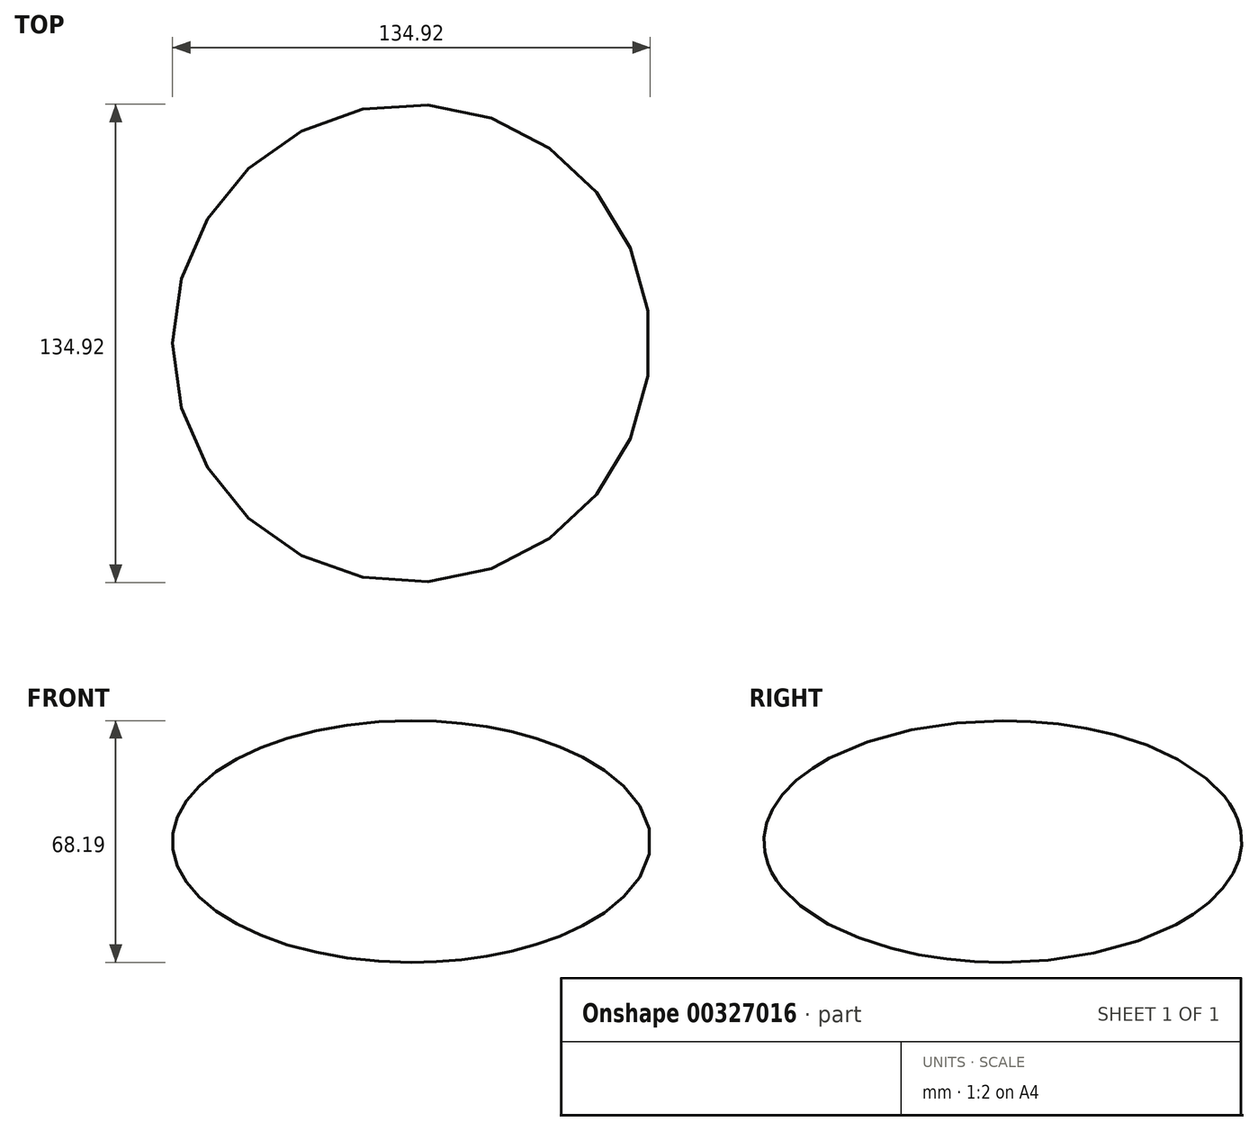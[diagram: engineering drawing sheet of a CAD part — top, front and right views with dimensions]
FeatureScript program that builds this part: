
annotation { "Feature Type Name" : "Feature", "Feature Type Description" : "" }
export const myFeature = defineFeature(function(context is Context, id is Id, definition is map)
    precondition{}
    {
        {
            var Q0;
            Q0=qCreatedBy(makeId("Front.planeOp"),FACE);
            var sketch = newSketch(context, id + "F0", { "sketchPlane" : qUnion([Q0])});
            skEllipse(sketch, "E0", {"center": v(0, 17.52) * mm, "majorRadius": 67.46 * mm, "minorRadius": 34.1 * mm, "majorAxis": v(1, 0)});
            skLineSegment(sketch, "E1", {"start": v(0, -16.57) * mm, "end": v(0, 51.62) * mm});
            skSolve(sketch);
        }
        {
            var Q0;
            {var subQ0=sQuery(id+"F0.wireOp",EDGE,"E1");Q0=makeQuery(id+"F0.imprint","IMPRINT",FACE,{"disambiguationData":[TD([[makeQuery(id+"F0.imprint","IMPRINT",EDGE,{"derivedFrom":subQ0}),1.0]])]});}
            var Q1;
            Q1=sQuery(id+"F0.wireOp",EDGE,"E1");
            revolve(context, id + "F1", {"entities" : qUnion([Q0]), "axis" : qUnion([Q1]), "revolveType" : RevolveType.FULL});
        }
    });
